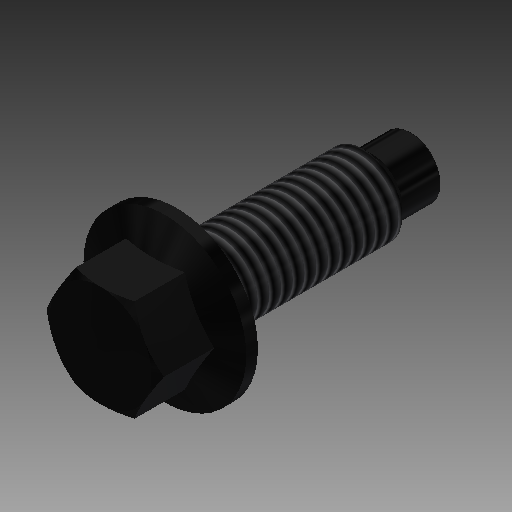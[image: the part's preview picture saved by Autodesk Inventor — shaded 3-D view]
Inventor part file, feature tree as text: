
AUTODESK INVENTOR PART (.ipt)
format: ipt  version: 2019 (Build 230136000, 136)  size: 181,760 bytes
history: native  units: mm
features: sketch x3, revolve x2, extrude x1, thread x1, fillet x1, projected_geometry x1
ambient origin geometry x8: Origin, YZ Plane, XZ Plane, XY Plane, X Axis, Y Axis, Z Axis, Center Point
bodies: Solid1 (feature_tree)
feature tree (9):
  extrude  "Extrusion1"  Depth=9.7mm TaperAngle=0.0deg
  revolve  "Revolution1"  [1 undecoded]
  revolve  "Revolution2"  [1 undecoded]
  thread  "Thread1"  [1 undecoded]
  fillet  "Fillet1"  Radius=30.0mm
  sketch  "Sketch1"  dims[d0=13.0mm d1=9.7mm d2=0.0mm]
  sketch  "Sketch2"  dims[d3=1.5mm d4=10.4mm]
  projected_geometry  "Projected Loop1"
  sketch  "Sketch3"  dims[d5=22.5deg d7=5.0mm d8=3.85mm d9=30.0mm d10=5.0mm d11=1.15mm d12=90.0deg d13=30.0deg d14=1.005553mm d16=6.5mm d17=90.0deg d18=10.0mm d19=0.0mm d20=0.2mm]
note: 3 required parameter values undecoded (feature->parameter linkage not recoverable at this tier; creation-order binding heuristic only, values carry confidence <= 0.55)